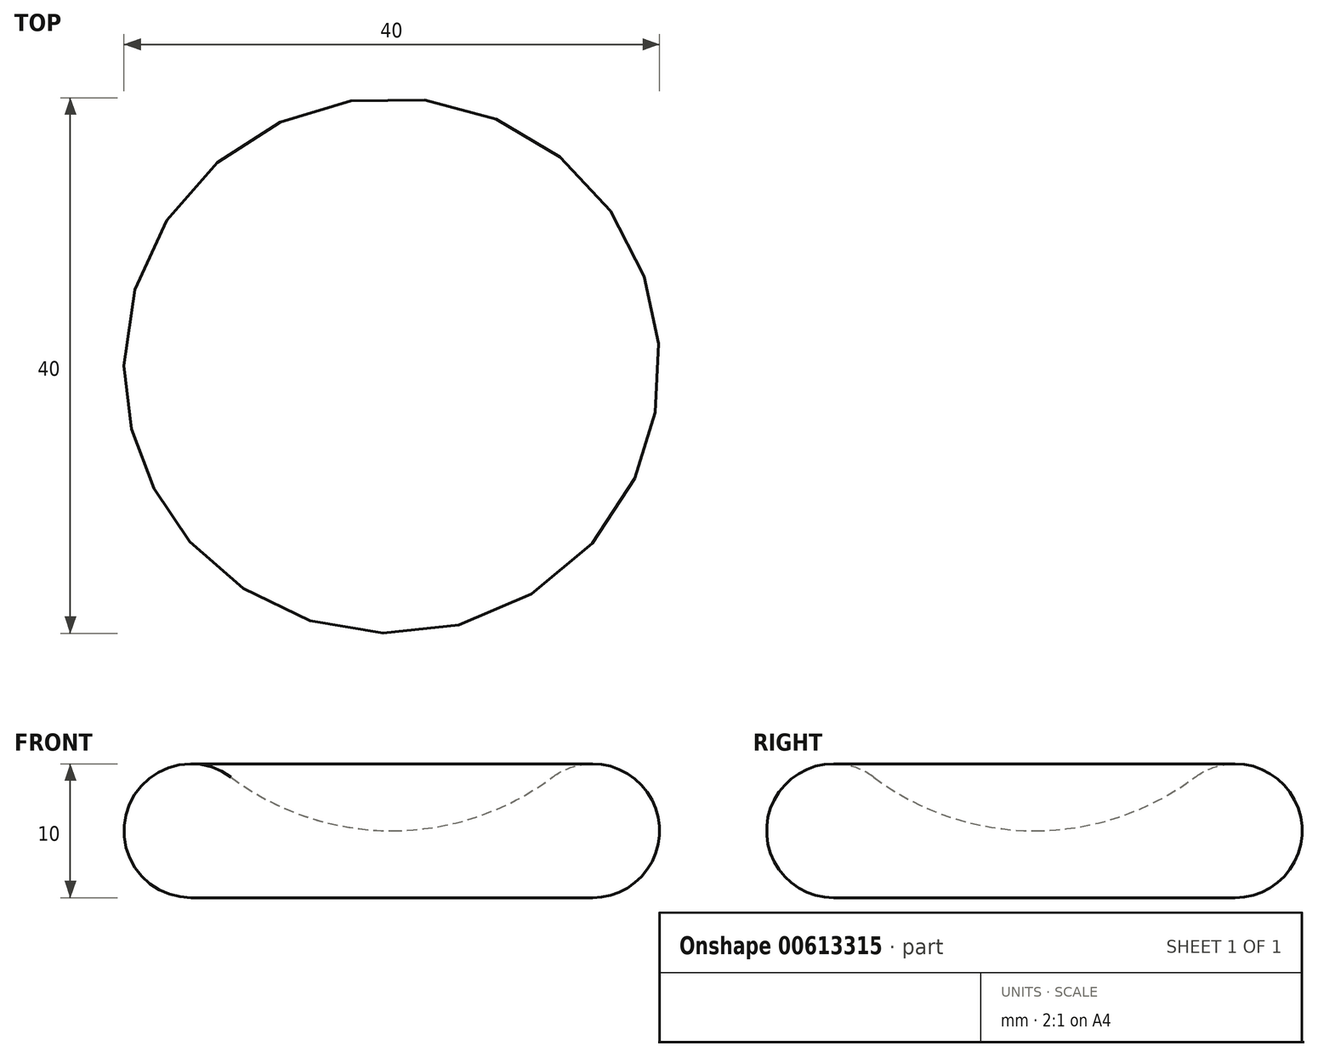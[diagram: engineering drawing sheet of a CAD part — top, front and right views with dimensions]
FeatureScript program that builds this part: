
annotation { "Feature Type Name" : "Feature", "Feature Type Description" : "" }
export const myFeature = defineFeature(function(context is Context, id is Id, definition is map)
    precondition{}
    {
        {
            var Q0;
            Q0=qCreatedBy(makeId("Front.planeOp"),FACE);
            var sketch = newSketch(context, id + "F0", { "sketchPlane" : qUnion([Q0])});
            skArc(sketch, "E0", {"start": v(-12, 9) * mm, "mid": v(-19.74, 6.58) * mm, "end": v(-15, 0) * mm});
            skArc(sketch, "E1", {"start": v(-12, 9) * mm, "mid": v(-6.32, 6.03) * mm, "end": v(0, 5) * mm});
            skLineSegment(sketch, "E2", {"start": v(0, 0) * mm, "end": v(-15, 0) * mm});
            skLineSegment(sketch, "E3", {"start": v(0, 0) * mm, "end": v(0, 5) * mm});
            skSolve(sketch);
        }
        {
            var Q0;
            Q0=makeQuery(id+"F0.imprint","IMPRINT",FACE,{"disambiguationData":[TD([[makeQuery(id+"F0.imprint","IMPRINT",EDGE,{"derivedFrom":sQuery(id+"F0.wireOp",EDGE,"E0")}),1.0]])]});
            var Q1;
            Q1=sQuery(id+"F0.wireOp",EDGE,"E3");
            revolve(context, id + "F1", {"entities" : qUnion([Q0]), "axis" : qUnion([Q1]), "revolveType" : RevolveType.FULL});
        }
    });
